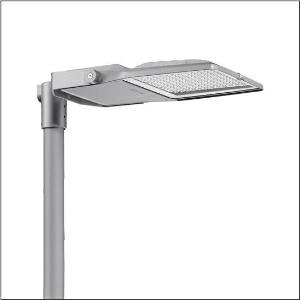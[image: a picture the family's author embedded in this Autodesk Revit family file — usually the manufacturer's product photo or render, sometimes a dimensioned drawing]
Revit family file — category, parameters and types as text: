
# Revit family: floodlight_fl_21_iq_midi___pl52_5xa7781f4d3a_7000
name_source: partatom
category: Lighting Fixtures
units: mm (PartAtom-declared; Revit-internal decimal feet)

## family parameters
Cut with Voids When Loaded = No
Host = Face
Light Source = No
Part Type = Normal
Room Calculation Point = No
Round Connector Dimension = Use Diameter
Shared = No

## types (1)
- --- (1 x LED, 37330 lm, 270.2 W, 4000K)
    Apparent Load = 270 VA
    CIE Flux Codes = 26 60 98 100 100
    Color Rendering = 70
    Color Temperature = 4000K
    Default Elevation = 1800 mm
    Description = Floodlight FL 21 iQ midi, floodlight, primary light control with lens, of PMMA, primary optical cover: protective disc, of toughened safety glass, transparent, light distribution: PL52, light emission: direct distribution, installation type: surface-mounted, LED, High Power LED, rated luminous flux: 37.330lm, luminous efficacy: 138lm/W, light colour: 740, colour temperature: 4000K, control gear: ECG iQ, control: optimised constant luminous flux control (CLO 2.0), Desk-Remote (wireless, voltage-free reading and setting of iQ features in the workshop via application-optimized NFC function/RFID function), Light-Fading, Smart-Wire, Night-Set, Lumen-Switch, Temp-Guard, Auto-Match, with terminal, 6-pole, mains connection: 220..240V, AC, 50/60Hz, start of lifetime: 270W, end of service life: 287W, reduction: 118W, luminaire housing, of diecast aluminium, powder-coated, Siteco® metallic grey (DB 702S), corrosivity category C5 mid according to DIN EN ISO 12944, sealing non-destructively replaceable, please order mast flange separately, mast bracket, of steel, galvanised, powder-coated, Siteco® metallic grey (DB 702S), protection rating (complete): IP66, insulation class (complete): insulation class II (safety insulation), certification: CE, protection symbol: D, impact resistance: IK08, permissible operating ambient temperature: -40..+40°C, permissible operating ambient temperature for outdoor applications: -40..+50°C, standard: DIN EN 12944, LABS conformity tested according to VDMA 24364:2018-05, packaging unit: 1 piece

Light Distribution: PL52
    Height = 76 mm
    Lamp = 1 x LED
    Lamp Light Flux = 37330 lm
    Lamp Power = 270.2 W
    Lamp count = 1
    Length = 657 mm
    Luminous efficacy = 138 lm/W
    Manufacturer = Siteco
    ModVariant = No
    Model = 5XA7781F4D3A
    Number of Poles = 1
    OnlyDefault = Yes
    Power Factor = 1
    Product Name = Floodlight FL 21 iQ midi | PL52
    Product group = floodlight | pylon annexe
    ProductGroupID = 6200
    Protection Class = Protection class II
    Protection Degree = IP 66
    RLX_Detail_Level = 1
    RLX_Emergency_Light_Flux = 0 lm
    RLX_Emergency_Type = 0
    RLX_Emergency_Type_DB = No
    RlxData = <blob elided: 153797 chars, md5=7c8b51f3>
    Socket = socket
    Standby Power = 0 W
    System Light Flux = 37330 lm
    System Power = 270 W
    Type Comments = factory setting: luminous flux: 100 % | dim-lin: 254 | 620 mA
    Type Image = l_1007123.jpg
    URL = http://relux.com
    VarID = @adj_035877
    Voltage = 0 V
    Weight = 0.00 kg
    Width = 442 mm

## geometry (parser evidence)
native form markers: Blend x4, Sweep x15
no freeform markers — native parametric forms only
